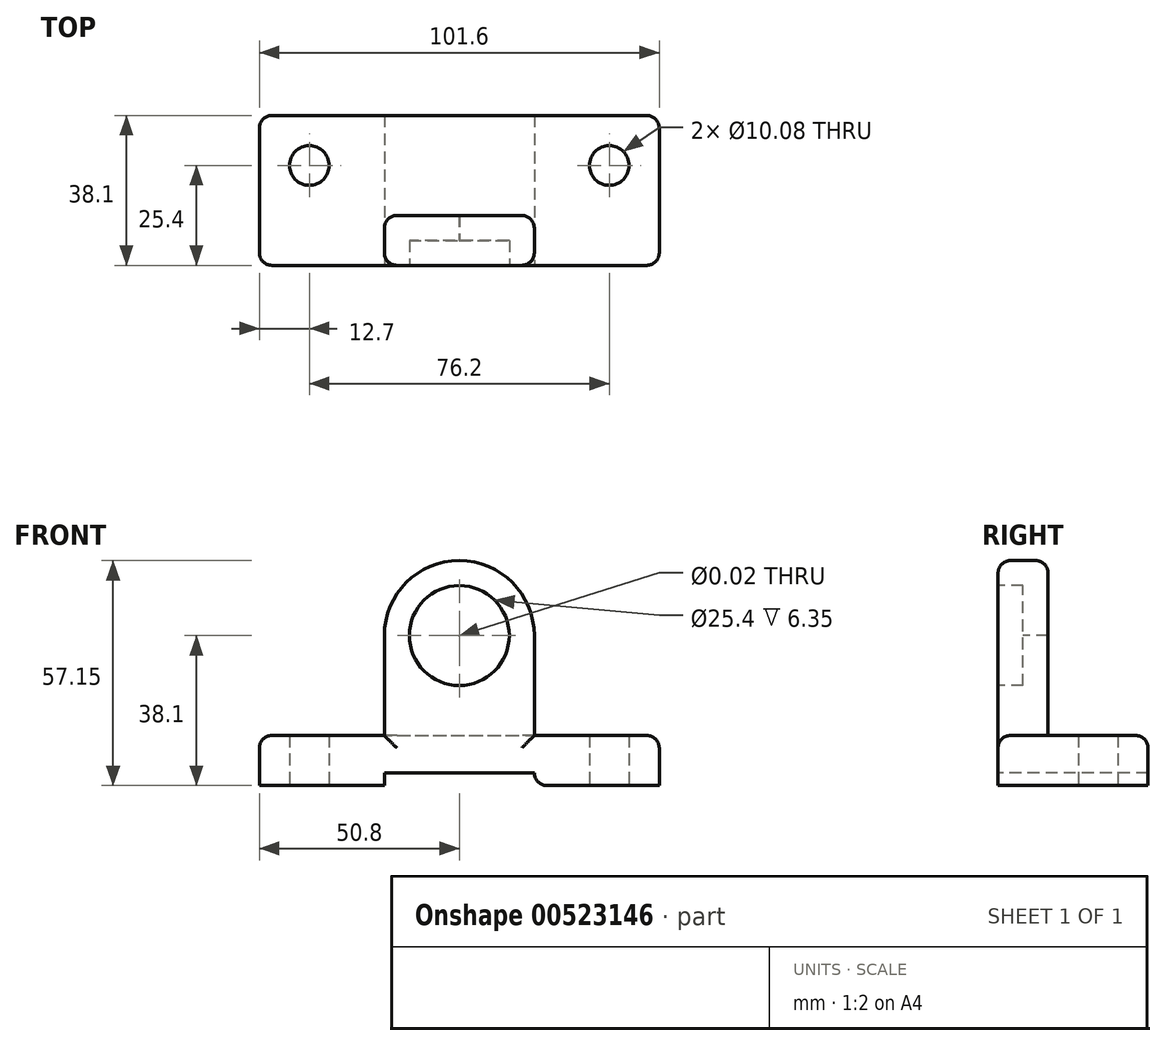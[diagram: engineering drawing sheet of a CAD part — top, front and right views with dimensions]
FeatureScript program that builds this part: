
annotation { "Feature Type Name" : "Feature", "Feature Type Description" : "" }
export const myFeature = defineFeature(function(context is Context, id is Id, definition is map)
    precondition{}
    {
        {
            var Q0;
            Q0=qCreatedBy(makeId("Top.planeOp"),FACE);
            var sketch = newSketch(context, id + "F0", { "sketchPlane" : qUnion([Q0])});
            skLineSegment(sketch, "E0.bottom", {"start": v(0, 0) * mm, "end": v(101.6, 0) * mm});
            skLineSegment(sketch, "E0.top", {"start": v(0, 38.1) * mm, "end": v(101.6, 38.1) * mm});
            skLineSegment(sketch, "E0.left", {"start": v(0, 0) * mm, "end": v(0, 38.1) * mm});
            skLineSegment(sketch, "E0.right", {"start": v(101.6, 0) * mm, "end": v(101.6, 38.1) * mm});
            skSolve(sketch);
        }
        {
            var Q0;
            Q0 = qSketchRegion(id + "F0", true);
            extrude(context, id + "F1", {"entities" : qUnion([Q0]), "depth" : 12.7 * mm, "offsetDistance" : 25.4 * mm});
        }
        {
            var Q0;
            Q0=makeQuery(id+"F1.opExtrude","SWEPT_FACE",FACE,{"disambiguationData":[OSD([sQuery(id+"F0.wireOp",EDGE,"E0.bottom")])]});
            var sketch = newSketch(context, id + "F2", { "sketchPlane" : qUnion([Q0])});
            skLineSegment(sketch, "E1", {"start": v(31.75, 0) * mm, "end": v(31.75, 38.1) * mm});
            skLineSegment(sketch, "E2", {"start": v(69.85, 38.1) * mm, "end": v(69.85, 0) * mm});
            skArc(sketch, "E3", {"start": v(69.85, 38.1) * mm, "mid": v(50.8, 57.15) * mm, "end": v(31.75, 38.1) * mm});
            skSolve(sketch);
        }
        {
            var Q0;
            Q0 = qSketchRegion(id + "F2", true);
            var Q1;
            {var subQ0=sQuery(id+"F2.wireOp",EDGE,"E3");Q1=makeQuery(id+"F2.imprint","IMPRINT",FACE,{"disambiguationData":[TD([[makeQuery(id+"F2.imprint","IMPRINT",EDGE,{"derivedFrom":subQ0}),1.0]])]});}
            extrude(context, id + "F3", {"entities" : qUnion([Q0, Q1]), "operationType" : NewBodyOperationType.ADD, "oppositeDirection" : true, "depth" : 12.7 * mm, "offsetDistance" : 25.4 * mm});
        }
        {
            var Q0;
            Q0=sQuery(id+"F2.wireOp",VERTEX,"E3.center");
            var Q1;
            Q1=makeQuery(id+"F1.opExtrude","SWEPT_BODY",BODY,{"disambiguationData":[OSD([sQuery(id+"F0.wireOp",EDGE,"E0.bottom"),sQuery(id+"F0.wireOp",EDGE,"E0.top"),sQuery(id+"F0.wireOp",EDGE,"E0.left"),sQuery(id+"F0.wireOp",EDGE,"E0.right")])]});
            hole(context, id + "F4", {"style" : HoleStyle.C_BORE, "endStyle" : HoleEndStyle.THROUGH, "standardTappedOrClearance" : lookupTablePath({ "standard" : "ANSI", "size" : "15/32 (0.47)", "type" : "Drilled" }), "standardBlindInLast" : lookupTablePath({ "standard" : "ANSI", "size" : "15/32", "type" : "Drilled" }), "holeDiameter" : 15 / 812.8 * mm, "cBoreDiameter" : 25.4 * mm, "cBoreDepth" : 6.35 * mm, "isTappedThrough" : true, "tappedDepth" : 12.7 * mm, "tapClearance" : 3, "locations" : qUnion([Q0]), "scope" : qUnion([Q1])});
        }
        {
            var Q0;
            Q0=qCreatedBy(makeId("Front.planeOp"),FACE);
            var sketch = newSketch(context, id + "F5", { "sketchPlane" : qUnion([Q0])});
            skLineSegment(sketch, "E4", {"start": v(31.75, 0) * mm, "end": v(31.75, 3.18) * mm});
            skLineSegment(sketch, "E5", {"start": v(31.75, 3.18) * mm, "end": v(69.85, 3.18) * mm});
            skLineSegment(sketch, "E6", {"start": v(69.85, 3.18) * mm, "end": v(69.85, 0) * mm});
            skLineSegment(sketch, "E7", {"start": v(69.85, 0) * mm, "end": v(31.75, 0) * mm});
            skSolve(sketch);
        }
        {
            var Q0;
            Q0 = qSketchRegion(id + "F5", true);
            extrude(context, id + "F6", {"entities" : qUnion([Q0]), "operationType" : NewBodyOperationType.REMOVE, "endBound" : BoundingType.THROUGH_ALL, "oppositeDirection" : true, "depth" : 25.4 * mm, "offsetDistance" : 25.4 * mm});
        }
        {
            var Q0;
            Q0=qCreatedBy(makeId("Top.planeOp"),FACE);
            var sketch = newSketch(context, id + "F7", { "sketchPlane" : qUnion([Q0])});
            skPoint(sketch, "E8", {"position": v(12.7, 25.4) * mm});
            skPoint(sketch, "E9", {"position": v(88.9, 25.4) * mm});
            skSolve(sketch);
        }
        {
            var Q0;
            Q0=sQuery(id+"F7.wireOp",VERTEX,"E8");
            var Q1;
            Q1=makeQuery(id+"F1.opExtrude","SWEPT_BODY",BODY,{"disambiguationData":[OSD([sQuery(id+"F0.wireOp",EDGE,"E0.bottom"),sQuery(id+"F0.wireOp",EDGE,"E0.top"),sQuery(id+"F0.wireOp",EDGE,"E0.left"),sQuery(id+"F0.wireOp",EDGE,"E0.right")])]});
            hole(context, id + "F8", {"style" : HoleStyle.SIMPLE, "endStyle" : HoleEndStyle.THROUGH, "oppositeDirection" : true, "standardTappedOrClearance" : lookupTablePath({ "standard" : "ANSI", "fit" : "Normal (ASME)", "size" : "3/8", "type" : "Clearance" }), "standardBlindInLast" : lookupTablePath({ "fit" : "Free", "standard" : "ANSI", "size" : "3/8", "type" : "Clearance" }), "holeDiameter" : 10.08 * mm, "isTappedThrough" : true, "tappedDepth" : 12.7 * mm, "tapClearance" : 3, "startFromSketch" : true, "locations" : qUnion([Q0]), "scope" : qUnion([Q1])});
        }
        {
            var Q0;
            Q0=sQuery(id+"F7.wireOp",VERTEX,"E9");
            var Q1;
            Q1=makeQuery(id+"F1.opExtrude","SWEPT_BODY",BODY,{"disambiguationData":[OSD([sQuery(id+"F0.wireOp",EDGE,"E0.bottom"),sQuery(id+"F0.wireOp",EDGE,"E0.top"),sQuery(id+"F0.wireOp",EDGE,"E0.left"),sQuery(id+"F0.wireOp",EDGE,"E0.right")])]});
            hole(context, id + "F9", {"style" : HoleStyle.SIMPLE, "endStyle" : HoleEndStyle.THROUGH, "oppositeDirection" : true, "standardTappedOrClearance" : lookupTablePath({ "standard" : "ANSI", "fit" : "Normal (ASME)", "size" : "3/8", "type" : "Clearance" }), "standardBlindInLast" : lookupTablePath({ "fit" : "Free", "standard" : "ANSI", "size" : "3/8", "type" : "Clearance" }), "holeDiameter" : 10.08 * mm, "isTappedThrough" : true, "tappedDepth" : 12.7 * mm, "tapClearance" : 3, "startFromSketch" : true, "locations" : qUnion([Q0]), "scope" : qUnion([Q1])});
        }
        {
            var Q0;
            Q0=makeQuery(id+"F1.opExtrude","SWEPT_EDGE",EDGE,{"disambiguationData":[OSD([sQuery(id+"F0.wireOp",EDGE,"E0.bottom"),sQuery(id+"F0.wireOp",EDGE,"E0.right")])]});
            var Q1;
            Q1=makeQuery(id+"F1.opExtrude","SWEPT_EDGE",EDGE,{"disambiguationData":[OSD([sQuery(id+"F0.wireOp",EDGE,"E0.top"),sQuery(id+"F0.wireOp",EDGE,"E0.right")])]});
            var Q2;
            Q2=makeQuery(id+"F1.opExtrude","SWEPT_EDGE",EDGE,{"disambiguationData":[OSD([sQuery(id+"F0.wireOp",EDGE,"E0.bottom"),sQuery(id+"F0.wireOp",EDGE,"E0.left")])]});
            var Q3;
            Q3=makeQuery(id+"F1.opExtrude","SWEPT_EDGE",EDGE,{"disambiguationData":[OSD([sQuery(id+"F0.wireOp",EDGE,"E0.top"),sQuery(id+"F0.wireOp",EDGE,"E0.left")])]});
            var Q4;
            Q4=makeQuery(id+"F6.boolean.opBoolean","COPY",EDGE,{"derivedFrom":makeQuery(id+"F6.opExtrude","SWEPT_EDGE",EDGE,{"disambiguationData":[OSD([sQuery(id+"F5.wireOp",EDGE,"E4"),sQuery(id+"F5.wireOp",EDGE,"E7")])]})});
            var Q5;
            Q5=makeQuery(id+"F6.boolean.opBoolean","COPY",EDGE,{"derivedFrom":makeQuery(id+"F6.opExtrude","SWEPT_EDGE",EDGE,{"disambiguationData":[OSD([sQuery(id+"F5.wireOp",EDGE,"E6"),sQuery(id+"F5.wireOp",EDGE,"E7")])]})});
            fillet(context, id + "F10", {"entities" : qUnion([Q0, Q1, Q2, Q3, Q4, Q5]), "radius" : 3.17 * mm, "tangentPropagation" : true, "allowEdgeOverflow" : false});
        }
        {
            var Q0;
            {var subQ1=sQuery(id+"F0.wireOp",EDGE,"E0.left");var subQ2=sQuery(id+"F0.wireOp",EDGE,"E0.bottom");Q0=makeQuery(id+"F3.boolean.opBoolean","SPLIT",EDGE,{"disambiguationData":[TD([makeQuery(id+"F1.opExtrude","SWEPT_FACE",FACE,{"disambiguationData":[OSD([subQ1])]})])],"derivedFrom":makeQuery(id+"F1.opExtrude","CAP_EDGE",EDGE,{"disambiguationData":[OSD([subQ2])],"isStart":false})});}
            var Q1;
            Q1=makeQuery(id+"F1.opExtrude","CAP_EDGE",EDGE,{"disambiguationData":[OSD([sQuery(id+"F0.wireOp",EDGE,"E0.left")])],"isStart":false});
            var Q2;
            Q2=makeQuery(id+"F1.opExtrude","CAP_EDGE",EDGE,{"disambiguationData":[OSD([sQuery(id+"F0.wireOp",EDGE,"E0.top")])],"isStart":false});
            var Q3;
            Q3=makeQuery(id+"F1.opExtrude","CAP_EDGE",EDGE,{"disambiguationData":[OSD([sQuery(id+"F0.wireOp",EDGE,"E0.right")])],"isStart":false});
            var Q4;
            Q4=makeQuery(id+"F3.opExtrude","CAP_EDGE",EDGE,{"disambiguationData":[OSD([sQuery(id+"F2.wireOp",EDGE,"E3")])],"isStart":true});
            var Q5;
            Q5=makeQuery(id+"F3.opExtrude","CAP_EDGE",EDGE,{"disambiguationData":[OSD([sQuery(id+"F2.wireOp",EDGE,"E3")])],"isStart":false});
            var Q6;
            Q6=makeQuery(id+"F3.opExtrude","SWEPT_EDGE",EDGE,{"disambiguationData":[OSD([sQuery(id+"F0.wireOp",EDGE,"E0.bottom"),sQuery(id+"F2.wireOp",EDGE,"E1")])]});
            fillet(context, id + "F11", {"entities" : qUnion([Q0, Q1, Q2, Q3, Q4, Q5, Q6]), "radius" : 3.17 * mm, "tangentPropagation" : true, "allowEdgeOverflow" : false});
        }
    });
